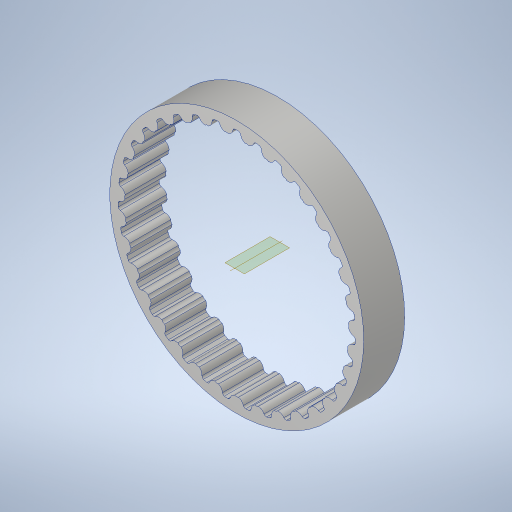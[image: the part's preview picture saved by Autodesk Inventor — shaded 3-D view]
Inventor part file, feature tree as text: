
AUTODESK INVENTOR PART (.ipt)
format: ipt  version: 2023.3 (Build 273359000, 359)  size: 782,848 bytes
history: native  units: in
note: dims shown in document units (in); Inventor stores cm internally (conversion verified against a paired STEP export)
features: extrude x3, sketch x3, projected_geometry x3, plane x1, other x1, pattern_circular x1
ambient origin geometry x8: Origin, YZ Plane, XZ Plane, XY Plane, X Axis, Y Axis, Z Axis, Center Point
bodies: Solid1 (feature_tree)
feature tree (12):
  extrude  "Extrusion1"  Depth=0.0197in
  plane  "Work Plane1"
  sketch  "Sketch2"  dims[d3=0.0591in]
  other  "Work Axis1"
  pattern_circular  "Circular Pattern1"  [2 undecoded]
  sketch  "Sketch3"  dims[d4=0.0328in d5=0.0591in d6=0.0197in d7=0.0748in d8=0.0945in d9=0.0762in d10=0.0762in d11=0.0655in d12=0.0197in d13=0.0748in d14=0.0in d15=0.25in d16=0.0191in d17=0.0408in d18=0.0148in d19=0.042in d20=0.3543in d21=0.0in d22=-1.0965in d23=13.7795in d24=360.0deg d26=2.1931in d27=0.125in d28=0.0in d29=0.0in d30=1.0in d31=0.0in]
  extrude  "Extrusion2"  Depth=0.0197in
  extrude  "Extrusion3"  Depth=0.3543in
  sketch  "Sketch1"  dims[d1=0.0444in d2=0.0197in]
  projected_geometry  "Projected Loop1"
  projected_geometry  "Project Cut Edges1"
  projected_geometry  "Project Cut Edges2"
note: 2 required parameter values undecoded (feature->parameter linkage not recoverable at this tier; creation-order binding heuristic only, values carry confidence <= 0.55)
